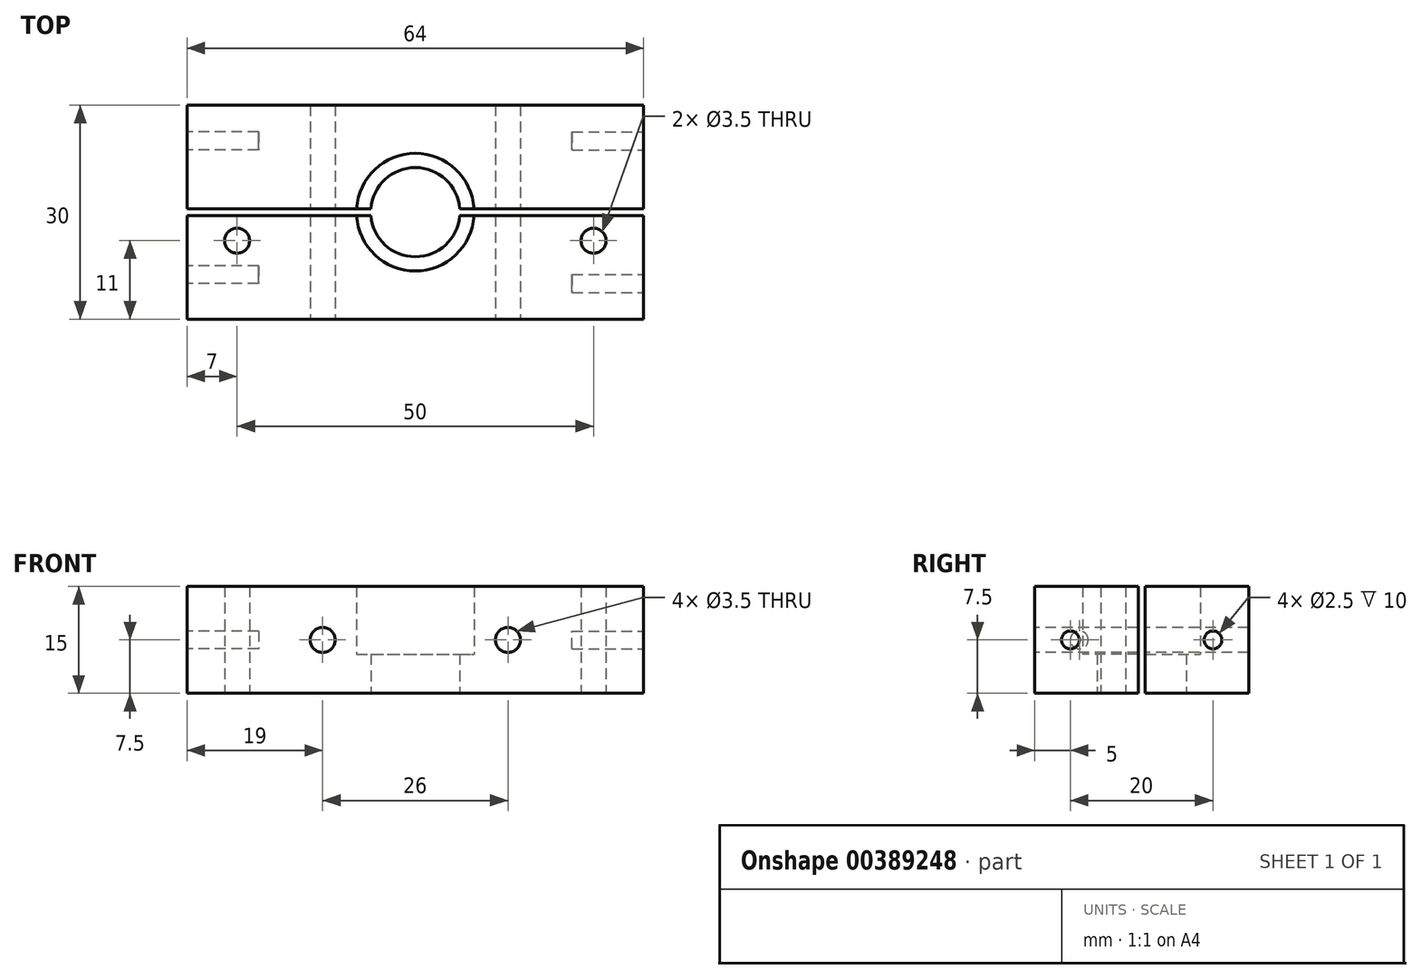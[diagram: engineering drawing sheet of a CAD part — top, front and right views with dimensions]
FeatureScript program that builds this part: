
annotation { "Feature Type Name" : "Feature", "Feature Type Description" : "" }
export const myFeature = defineFeature(function(context is Context, id is Id, definition is map)
    precondition{}
    {
        {
            var Q0;
            Q0=qCreatedBy(makeId("Top.planeOp"),FACE);
            var sketch = newSketch(context, id + "F0", { "sketchPlane" : qUnion([Q0])});
            skLineSegment(sketch, "E0.bottom", {"start": v(0, 0) * mm, "end": v(-64, 0) * mm});
            skLineSegment(sketch, "E0.top", {"start": v(0, 30) * mm, "end": v(-64, 30) * mm});
            skLineSegment(sketch, "E0.left", {"start": v(0, 0) * mm, "end": v(0, 30) * mm});
            skLineSegment(sketch, "E0.right", {"start": v(-64, 0) * mm, "end": v(-64, 30) * mm});
            skLineSegment(sketch, "E1", {"start": v(0, 15) * mm, "end": v(-64, 15) * mm, "construction": true});
            skLineSegment(sketch, "E2", {"start": v(-32, 0) * mm, "end": v(-32, 30) * mm, "construction": true});
            skCircle(sketch, "E3", {"center": v(-32, 15) * mm, "radius": 6.25 * mm});
            skCircle(sketch, "E4", {"center": v(-32, 15) * mm, "radius": 8.25 * mm});
            skCircle(sketch, "E5", {"center": v(-57, 11) * mm, "radius": 1.75 * mm});
            skCircle(sketch, "E6", {"center": v(-7, 11) * mm, "radius": 1.75 * mm});
            skSolve(sketch);
        }
        {
            var Q0;
            Q0 = qSketchRegion(id + "F0", true);
            extrude(context, id + "F1", {"entities" : qUnion([Q0]), "depth" : 15 * mm});
        }
        {
            var Q0;
            Q0=makeQuery(id+"F0.imprint","IMPRINT",FACE,{"disambiguationData":[TD([[makeQuery(id+"F0.imprint","IMPRINT",EDGE,{"derivedFrom":sQuery(id+"F0.wireOp",EDGE,"E3")}),-1.0]])]});
            extrude(context, id + "F2", {"entities" : qUnion([Q0]), "operationType" : NewBodyOperationType.ADD, "depth" : 5.5 * mm});
        }
        {
            var Q0;
            Q0=makeQuery(id+"F1.opExtrude","SWEPT_FACE",FACE,{"disambiguationData":[OSD([sQuery(id+"F0.wireOp",EDGE,"E0.left")])]});
            var sketch = newSketch(context, id + "F3", { "sketchPlane" : qUnion([Q0])});
            skLineSegment(sketch, "E7", {"start": v(15, 15) * mm, "end": v(15, 0) * mm, "construction": true});
            skLineSegment(sketch, "E8", {"start": v(14.5, 15) * mm, "end": v(14.5, 0) * mm});
            skLineSegment(sketch, "E9", {"start": v(15.5, 15) * mm, "end": v(15.5, 0) * mm});
            skSolve(sketch);
        }
        {
            var Q0;
            Q0 = qSketchRegion(id + "F3", true);
            var Q1;
            {var subQ0=sQuery(id+"F3.wireOp",EDGE,"E8");Q1=makeQuery(id+"F3.imprint","IMPRINT",FACE,{"disambiguationData":[TD([[makeQuery(id+"F3.imprint","IMPRINT",EDGE,{"derivedFrom":subQ0}),1.0]])]});}
            extrude(context, id + "F4", {"entities" : qUnion([Q0, Q1]), "operationType" : NewBodyOperationType.REMOVE, "endBound" : BoundingType.THROUGH_ALL, "oppositeDirection" : true, "depth" : 25 * mm});
        }
        {
            var Q0;
            Q0=makeQuery(id+"F1.opExtrude","SWEPT_FACE",FACE,{"disambiguationData":[OSD([sQuery(id+"F0.wireOp",EDGE,"E0.bottom")])]});
            var sketch = newSketch(context, id + "F5", { "sketchPlane" : qUnion([Q0])});
            skSolve(sketch);
        }
        {
            var Q0;
            {var subQ0=sQuery(id+"F0.wireOp",EDGE,"E0.bottom");Q0=makeQuery(id+"F5.imprint","IMPRINT",FACE,{"disambiguationData":[TD([[makeQuery(id+"F5.imprint","IMPRINT",EDGE,{"derivedFrom":makeQuery(id+"F1.opExtrude","CAP_EDGE",EDGE,{"disambiguationData":[OSD([subQ0])],"isStart":true})}),-1.0]])]});}
            var sketch = newSketch(context, id + "F6", { "sketchPlane" : qUnion([Q0])});
            skCircle(sketch, "E10", {"center": v(-45, 7.5) * mm, "radius": 1.75 * mm});
            skCircle(sketch, "E11", {"center": v(-19, 7.5) * mm, "radius": 1.75 * mm});
            skSolve(sketch);
        }
        {
            var Q0;
            Q0 = qSketchRegion(id + "F6", true);
            extrude(context, id + "F7", {"entities" : qUnion([Q0]), "operationType" : NewBodyOperationType.REMOVE, "endBound" : BoundingType.THROUGH_ALL, "oppositeDirection" : true, "depth" : 30 * mm});
        }
        {
            var Q0;
            {var subQ4=sQuery(id+"F0.wireOp",EDGE,"E0.left");var subQ6=sQuery(id+"F0.wireOp",EDGE,"E0.bottom");Q0=makeQuery(id+"F4.boolean.opBoolean","SPLIT",FACE,{"disambiguationData":[TD([makeQuery(id+"F1.opExtrude","SWEPT_FACE",FACE,{"disambiguationData":[OSD([subQ6])]})])],"derivedFrom":makeQuery(id+"F1.opExtrude","SWEPT_FACE",FACE,{"disambiguationData":[OSD([subQ4])]})});}
            var sketch = newSketch(context, id + "F8", { "sketchPlane" : qUnion([Q0])});
            skLineSegment(sketch, "E12", {"start": v(25.49, 7.5) * mm, "end": v(0, 7.5) * mm, "construction": true});
            skCircle(sketch, "E13", {"center": v(5, 7.5) * mm, "radius": 1.25 * mm});
            skCircle(sketch, "E14", {"center": v(25, 7.5) * mm, "radius": 1.25 * mm});
            skSolve(sketch);
        }
        {
            var Q0;
            Q0 = qSketchRegion(id + "F8", true);
            extrude(context, id + "F9", {"entities" : qUnion([Q0]), "operationType" : NewBodyOperationType.REMOVE, "oppositeDirection" : true, "depth" : 10 * mm});
        }
        {
            var Q0;
            {var subQ0=sQuery(id+"F0.wireOp",EDGE,"E0.top");var subQ4=sQuery(id+"F0.wireOp",EDGE,"E0.right");Q0=makeQuery(id+"F4.boolean.opBoolean","SPLIT",FACE,{"disambiguationData":[TD([makeQuery(id+"F1.opExtrude","SWEPT_FACE",FACE,{"disambiguationData":[OSD([subQ0])]})])],"derivedFrom":makeQuery(id+"F1.opExtrude","SWEPT_FACE",FACE,{"disambiguationData":[OSD([subQ4])]})});}
            var sketch = newSketch(context, id + "F10", { "sketchPlane" : qUnion([Q0])});
            skCircle(sketch, "E15", {"center": v(-25, 7.5) * mm, "radius": 1.25 * mm});
            skCircle(sketch, "E16", {"center": v(-6.25, 7.5) * mm, "radius": 1.25 * mm});
            skPoint(sketch, "E16.centerSnap0", {"position": v(-15.5, 7.5) * mm});
            skSolve(sketch);
        }
        {
            var Q0;
            Q0 = qSketchRegion(id + "F10", true);
            extrude(context, id + "F11", {"entities" : qUnion([Q0]), "operationType" : NewBodyOperationType.REMOVE, "oppositeDirection" : true, "depth" : 10 * mm});
        }
    });
